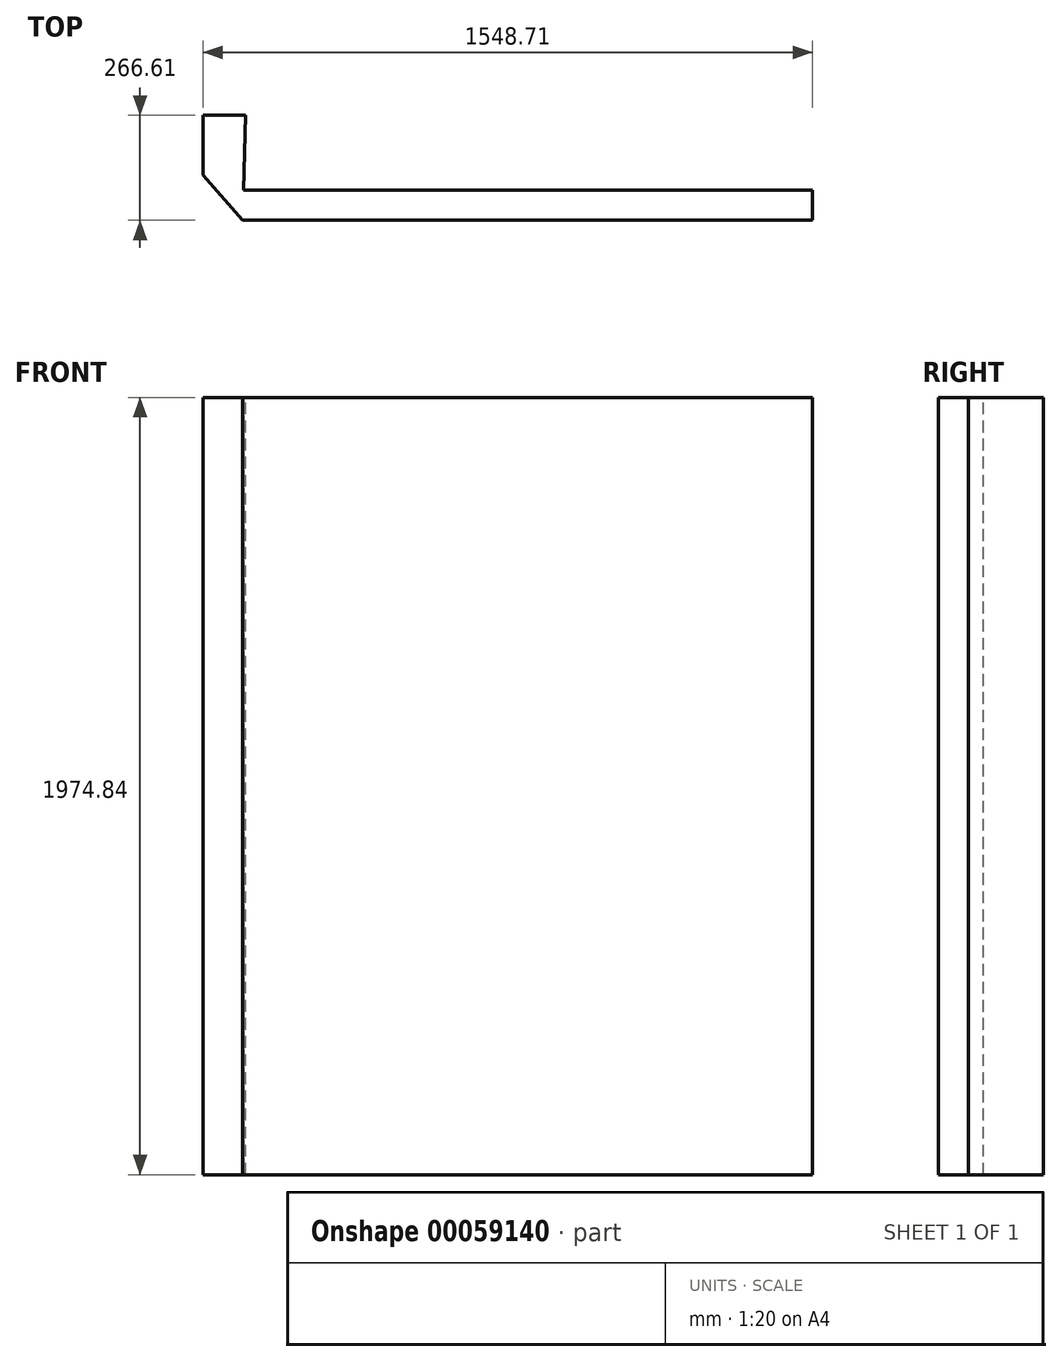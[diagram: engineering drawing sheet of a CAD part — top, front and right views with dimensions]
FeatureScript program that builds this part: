
annotation { "Feature Type Name" : "Feature", "Feature Type Description" : "" }
export const myFeature = defineFeature(function(context is Context, id is Id, definition is map)
    precondition{}
    {
        {
            var Q0;
            Q0=qCreatedBy(makeId("Front.planeOp"),FACE);
            var sketch = newSketch(context, id + "F0", { "sketchPlane" : qUnion([Q0])});
            skLineSegment(sketch, "E0.rect.bottom", {"start": v(723.9, 987.43) * mm, "end": v(-723.9, 987.43) * mm});
            skLineSegment(sketch, "E0.rect.top", {"start": v(723.9, -987.43) * mm, "end": v(-723.9, -987.43) * mm});
            skLineSegment(sketch, "E0.rect.left", {"start": v(723.9, 987.43) * mm, "end": v(723.9, -987.42) * mm});
            skLineSegment(sketch, "E0.rect.right", {"start": v(-723.9, 987.43) * mm, "end": v(-723.9, -987.43) * mm});
            skPoint(sketch, "E0.rect.middle", {"position": v(0, 0) * mm});
            skSolve(sketch);
        }
        {
            var Q0;
            Q0 = qSketchRegion(id + "F0", true);
            extrude(context, id + "F1", {"entities" : qUnion([Q0]), "oppositeDirection" : true, "depth" : 76.2 * mm});
        }
        {
            var Q0;
            Q0=makeQuery(id+"F1.opExtrude","SWEPT_FACE",FACE,{"disambiguationData":[OSD([sQuery(id+"F0.wireOp",EDGE,"E0.rect.bottom")])]});
            var sketch = newSketch(context, id + "F2", { "sketchPlane" : qUnion([Q0])});
            skLineSegment(sketch, "E1", {"start": v(-723.9, 0) * mm, "end": v(-824.8, 114.2) * mm});
            skLineSegment(sketch, "E2", {"start": v(-824.8, 114.2) * mm, "end": v(-824.8, 266.6) * mm});
            skLineSegment(sketch, "E3", {"start": v(-824.8, 266.6) * mm, "end": v(-716.86, 266.6) * mm});
            skLineSegment(sketch, "E4", {"start": v(-716.86, 266.6) * mm, "end": v(-723.9, 0) * mm});
            skSolve(sketch);
        }
        {
            var Q0;
            Q0 = qSketchRegion(id + "F2", true);
            extrude(context, id + "F3", {"entities" : qUnion([Q0]), "operationType" : NewBodyOperationType.ADD, "oppositeDirection" : true, "depth" : 1974.85 * mm});
        }
    });
